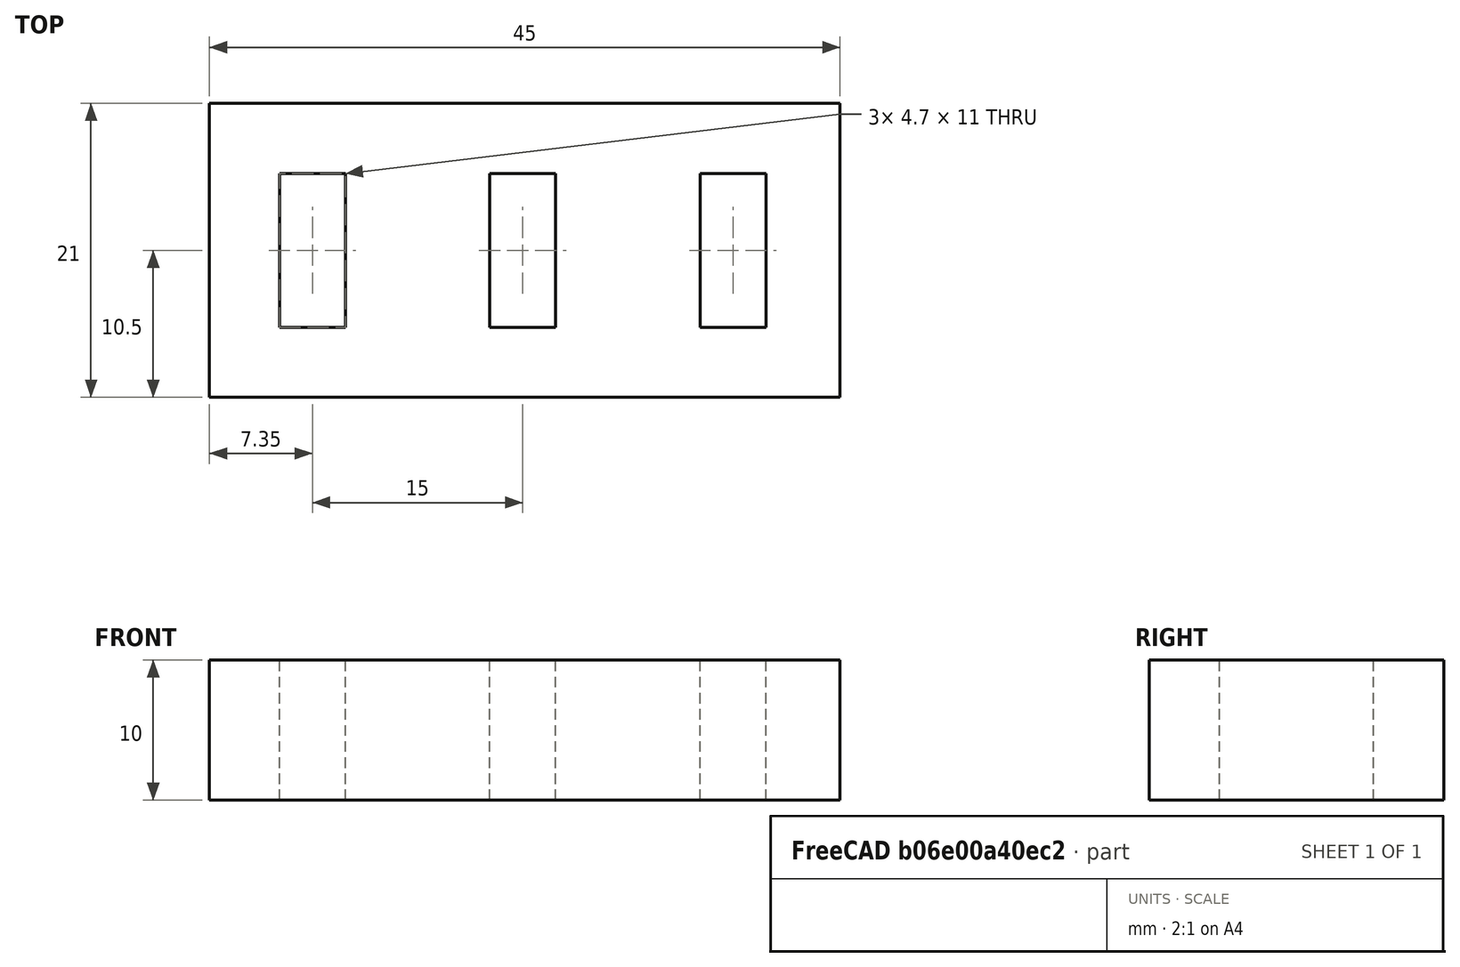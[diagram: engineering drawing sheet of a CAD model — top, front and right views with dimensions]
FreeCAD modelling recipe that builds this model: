
FCSTD DOCUMENT  (FreeCAD 0.21R33694 (Git))
Label: OJT1_T07P01-pens
License: All rights reserved
LicenseURL: http://en.wikipedia.org/wiki/All_rights_reserved
objects: Part::Box×4, Part::Cut×3
note: 7 computed .brp shape members not serialized (recipe doc carries the construction recipe); baked Part::Feature solids carry a one-line shape summary decoded from their .brp

FEATURE [Part::Box] Box  label="Cub"
  AttacherType = Attacher::AttachEngine3D
  Height = 10
  Length = 4.7
  Width = 11
FEATURE [Part::Box] Box001  label="Cub001"
  AttacherType = Attacher::AttachEngine3D
  Height = 10
  Length = 4.7
  Placement = pos=(15,0,0) rot=(0,0,1;0rad)
  Width = 11
FEATURE [Part::Box] Box002  label="Cub002"
  AttacherType = Attacher::AttachEngine3D
  Height = 10
  Length = 4.7
  Placement = pos=(30,0,0) rot=(0,0,1;0rad)
  Width = 11
FEATURE [Part::Box] Box003  label="Cub003"
  AttacherType = Attacher::AttachEngine3D
  Height = 10
  Length = 45
  Placement = pos=(-5,-5,0) rot=(0,0,1;0rad)
  Width = 21
FEATURE [Part::Cut] Cut
  Base = -> Box003
  Refine = true
  Tool = -> Box002
FEATURE [Part::Cut] Cut001
  Base = -> Cut
  Refine = true
  Tool = -> Box001
FEATURE [Part::Cut] Cut002
  Base = -> Cut001
  Refine = true
  Tool = -> Box
